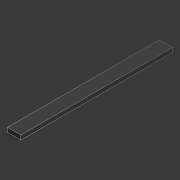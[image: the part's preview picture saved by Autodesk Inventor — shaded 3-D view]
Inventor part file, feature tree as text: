
AUTODESK INVENTOR PART (.ipt)
format: ipt  version: 2020.2 (Build 242310000, 310)  size: 91,136 bytes
history: native  units: mm
features: extrude x1, sketch x1
ambient origin geometry x8: Origin, YZ Plane, XZ Plane, XY Plane, X Axis, Y Axis, Z Axis, Center Point
bodies: Solid1 (feature_tree)
feature tree (2):
  extrude  "Extrusion1"  Depth=54.625mm
  sketch  "Sketch1"  dims[d0=4.7625mm d1=54.625mm d2=1.5875mm d3=0.0mm]
